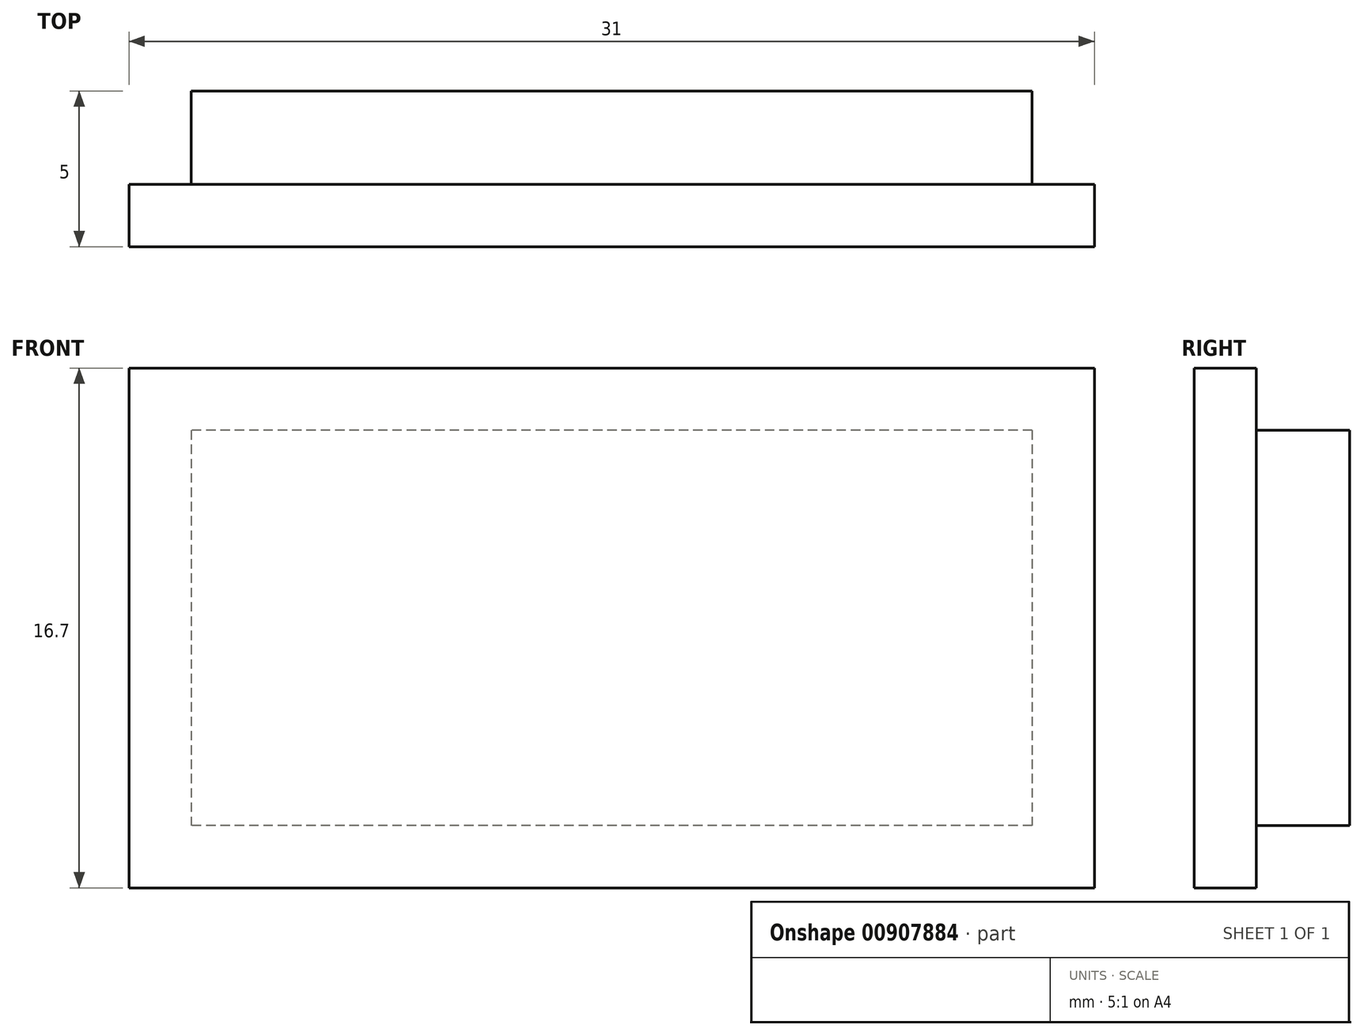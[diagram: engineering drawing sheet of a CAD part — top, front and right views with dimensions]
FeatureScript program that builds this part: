
annotation { "Feature Type Name" : "Feature", "Feature Type Description" : "" }
export const myFeature = defineFeature(function(context is Context, id is Id, definition is map)
    precondition{}
    {
        {
            var Q0;
            Q0=qCreatedBy(makeId("Front.planeOp"),FACE);
            var sketch = newSketch(context, id + "F0", { "sketchPlane" : qUnion([Q0])});
            skLineSegment(sketch, "E0.bottom", {"start": v(13.5, 6.35) * mm, "end": v(-13.5, 6.35) * mm});
            skLineSegment(sketch, "E0.top", {"start": v(13.5, -6.35) * mm, "end": v(-13.5, -6.35) * mm});
            skLineSegment(sketch, "E0.left", {"start": v(13.5, 6.35) * mm, "end": v(13.5, -6.35) * mm});
            skLineSegment(sketch, "E0.right", {"start": v(-13.5, 6.35) * mm, "end": v(-13.5, -6.35) * mm});
            skPoint(sketch, "E0.middle", {"position": v(0, 0) * mm});
            skLineSegment(sketch, "E1.0", {"start": v(-15.5, 8.35) * mm, "end": v(-15.5, -8.35) * mm});
            skLineSegment(sketch, "E1.1", {"start": v(15.5, 8.35) * mm, "end": v(-15.5, 8.35) * mm});
            skLineSegment(sketch, "E1.2", {"start": v(15.5, 8.35) * mm, "end": v(15.5, -8.35) * mm});
            skLineSegment(sketch, "E1.3", {"start": v(15.5, -8.35) * mm, "end": v(-15.5, -8.35) * mm});
            skSolve(sketch);
        }
        {
            var Q0;
            Q0=makeQuery(id+"F0.imprint","IMPRINT",FACE,{"disambiguationData":[TD([[makeQuery(id+"F0.imprint","IMPRINT",EDGE,{"derivedFrom":sQuery(id+"F0.wireOp",EDGE,"E0.bottom")}),-1.0]])]});
            extrude(context, id + "F1", {"entities" : qUnion([Q0]), "depth" : 2 * mm, "offsetDistance" : 25 * mm});
        }
        {
            var Q0;
            Q0=makeQuery(id+"F1.opExtrude","CAP_FACE",FACE,{"disambiguationData":[OSD([sQuery(id+"F0.wireOp",EDGE,"E0.bottom"),sQuery(id+"F0.wireOp",EDGE,"E0.top"),sQuery(id+"F0.wireOp",EDGE,"E0.left"),sQuery(id+"F0.wireOp",EDGE,"E0.right"),sQuery(id+"F0.wireOp",EDGE,"E1.0"),sQuery(id+"F0.wireOp",EDGE,"E1.1"),sQuery(id+"F0.wireOp",EDGE,"E1.2"),sQuery(id+"F0.wireOp",EDGE,"E1.3")])],"isStart":false});
            var sketch = newSketch(context, id + "F2", { "sketchPlane" : qUnion([Q0])});
            skSolve(sketch);
        }
        {
            var Q0;
            Q0=makeQuery(id+"F2.imprint","IMPRINT",FACE,{"disambiguationData":[TD([[makeQuery(id+"F2.imprint","IMPRINT",EDGE,{"derivedFrom":makeQuery(id+"F1.opExtrude","CAP_EDGE",EDGE,{"disambiguationData":[OSD([sQuery(id+"F0.wireOp",EDGE,"E0.bottom")])],"isStart":false})}),1.0]])]});
            extrude(context, id + "F3", {"entities" : qUnion([Q0]), "operationType" : NewBodyOperationType.ADD, "oppositeDirection" : true, "depth" : 5 * mm, "offsetDistance" : 25 * mm});
        }
    });
